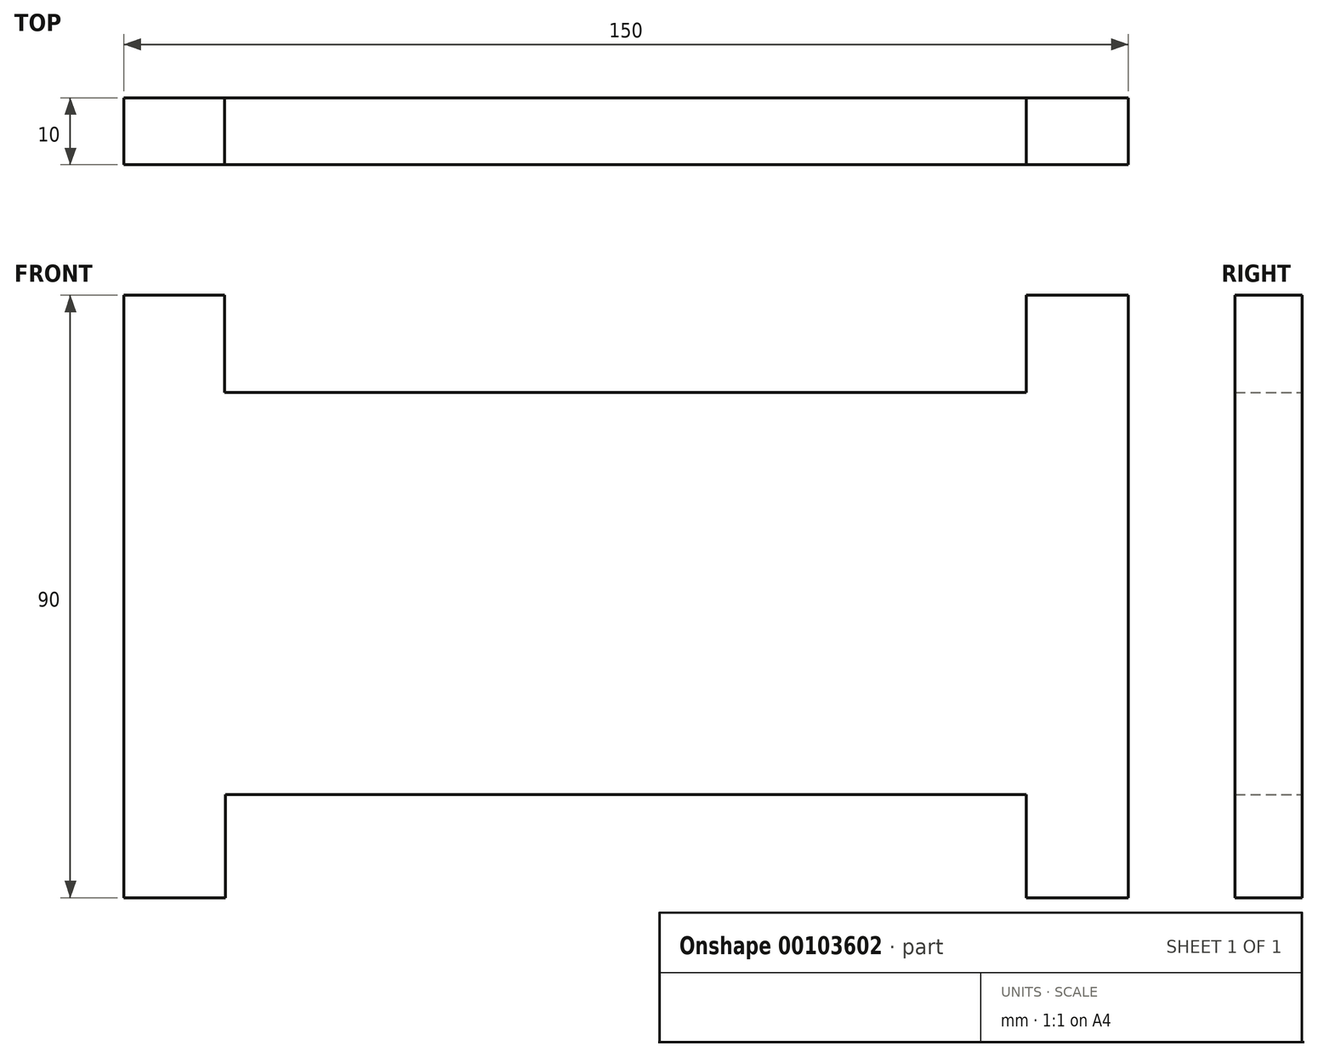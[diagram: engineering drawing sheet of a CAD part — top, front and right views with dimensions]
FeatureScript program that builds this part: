
annotation { "Feature Type Name" : "Feature", "Feature Type Description" : "" }
export const myFeature = defineFeature(function(context is Context, id is Id, definition is map)
    precondition{}
    {
        {
            var Q0;
            Q0=qCreatedBy(makeId("Front.planeOp"),FACE);
            var sketch = newSketch(context, id + "F0", { "sketchPlane" : qUnion([Q0])});
            skLineSegment(sketch, "E0.left", {"start": v(75, -45) * mm, "end": v(75, 45) * mm});
            skLineSegment(sketch, "E0.right", {"start": v(-75, -45) * mm, "end": v(-75, 45) * mm});
            skPoint(sketch, "E0.middle", {"position": v(0, 0) * mm});
            skLineSegment(sketch, "E1.top", {"start": v(-59.84, -29.58) * mm, "end": v(59.77, -29.58) * mm});
            skLineSegment(sketch, "E1.left", {"start": v(-59.84, -45) * mm, "end": v(-59.84, -29.58) * mm});
            skLineSegment(sketch, "E1.right", {"start": v(59.77, -45) * mm, "end": v(59.77, -29.58) * mm});
            skLineSegment(sketch, "E2", {"start": v(-75, -45) * mm, "end": v(-59.84, -45) * mm});
            skLineSegment(sketch, "E3", {"start": v(59.77, -45) * mm, "end": v(75, -45) * mm});
            skLineSegment(sketch, "E4.top", {"start": v(-60, 30.45) * mm, "end": v(59.77, 30.45) * mm});
            skLineSegment(sketch, "E4.left", {"start": v(-60, 45) * mm, "end": v(-60, 30.45) * mm});
            skLineSegment(sketch, "E4.right", {"start": v(59.77, 45) * mm, "end": v(59.77, 30.45) * mm});
            skLineSegment(sketch, "E5", {"start": v(-75, 45) * mm, "end": v(-60, 45) * mm});
            skLineSegment(sketch, "E6", {"start": v(59.77, 45) * mm, "end": v(75, 45) * mm});
            skSolve(sketch);
        }
        {
            var Q0;
            Q0=makeQuery(id+"F0.imprint","IMPRINT",FACE,{"disambiguationData":[TD([[makeQuery(id+"F0.imprint","IMPRINT",EDGE,{"derivedFrom":sQuery(id+"F0.wireOp",EDGE,"E0.left")}),1.0]])]});
            extrude(context, id + "F1", {"entities" : qUnion([Q0]), "depth" : 10 * mm});
        }
    });
